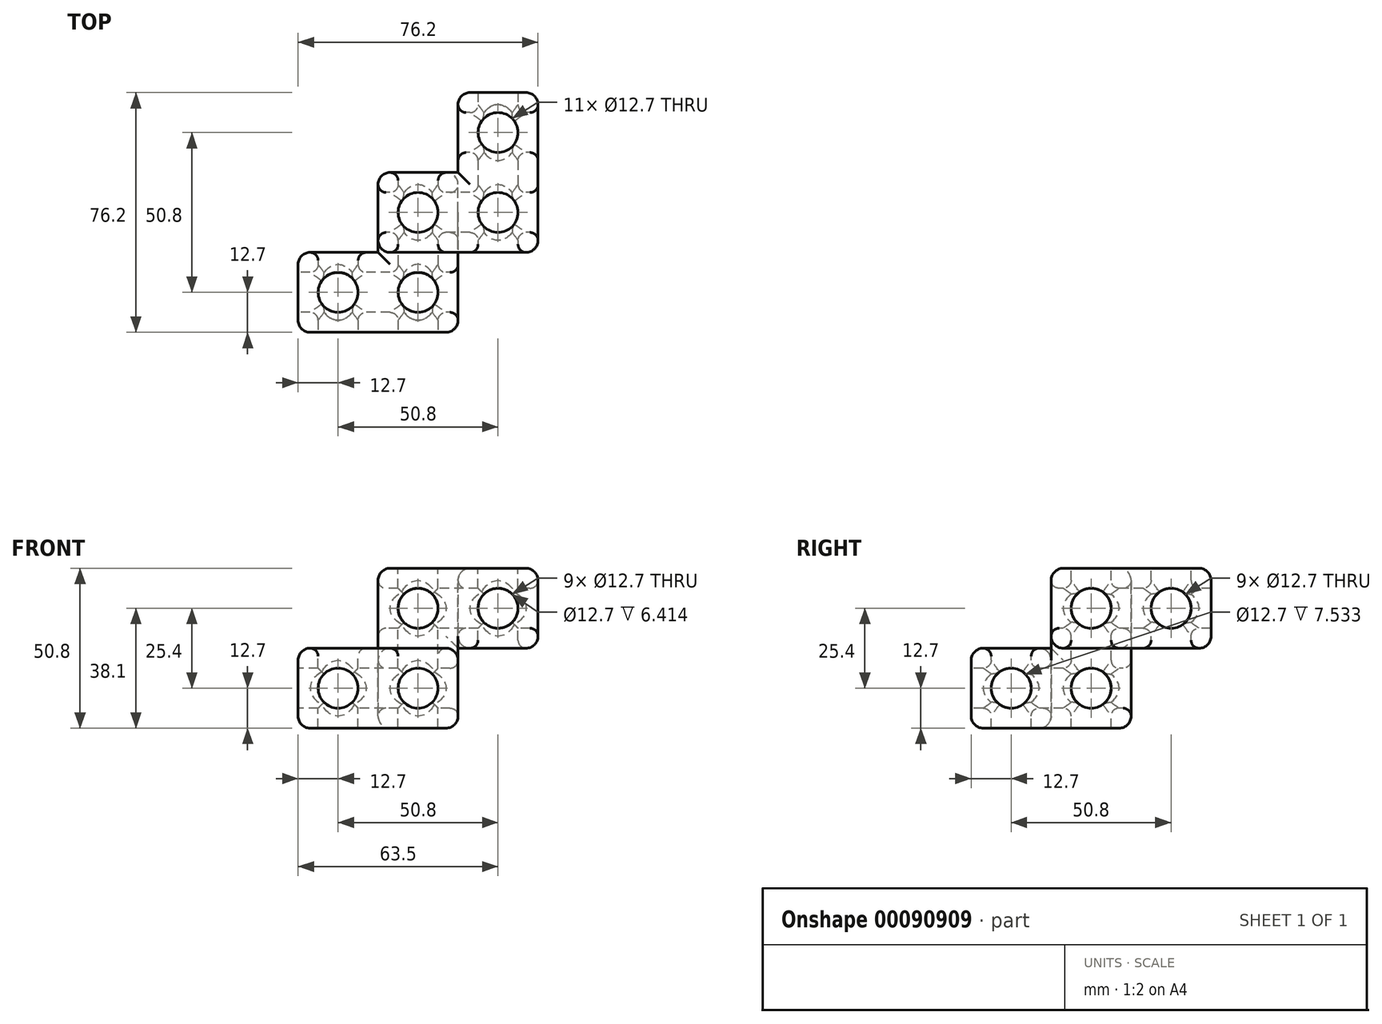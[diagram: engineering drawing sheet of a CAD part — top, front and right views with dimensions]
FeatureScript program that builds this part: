
annotation { "Feature Type Name" : "Feature", "Feature Type Description" : "" }
export const myFeature = defineFeature(function(context is Context, id is Id, definition is map)
    precondition{}
    {
        {
            var Q0;
            Q0=qCreatedBy(makeId("Top.planeOp"),FACE);
            var sketch = newSketch(context, id + "F0", { "sketchPlane" : qUnion([Q0])});
            skLineSegment(sketch, "E0.bottom", {"start": v(0, 0) * mm, "end": v(50.8, 0) * mm});
            skLineSegment(sketch, "E0.right", {"start": v(50.8, 0) * mm, "end": v(50.8, 50.8) * mm});
            skLineSegment(sketch, "E1", {"start": v(0, 25.4) * mm, "end": v(25.4, 25.4) * mm});
            skPoint(sketch, "E1.endSnap0", {"position": v(25.4, 0) * mm});
            skLineSegment(sketch, "E2", {"start": v(25.4, 25.4) * mm, "end": v(25.4, 50.8) * mm});
            skLineSegment(sketch, "E3", {"start": v(0, 0) * mm, "end": v(0, 25.4) * mm});
            skLineSegment(sketch, "E4", {"start": v(25.4, 50.8) * mm, "end": v(50.8, 50.8) * mm});
            skSolve(sketch);
        }
        {
            var Q0;
            Q0 = qSketchRegion(id + "F0", true);
            extrude(context, id + "F1", {"entities" : qUnion([Q0]), "depth" : 25.4 * mm});
        }
        {
            var Q0;
            Q0=makeQuery(id+"F1.opExtrude","CAP_FACE",FACE,{"disambiguationData":[OSD([sQuery(id+"F0.wireOp",EDGE,"E0.bottom"),sQuery(id+"F0.wireOp",EDGE,"E0.right"),sQuery(id+"F0.wireOp",EDGE,"E1"),sQuery(id+"F0.wireOp",EDGE,"E2"),sQuery(id+"F0.wireOp",EDGE,"E3"),sQuery(id+"F0.wireOp",EDGE,"E4")])],"isStart":false});
            var sketch = newSketch(context, id + "F2", { "sketchPlane" : qUnion([Q0])});
            skLineSegment(sketch, "E5.bottom", {"start": v(25.4, 25.4) * mm, "end": v(76.2, 25.4) * mm});
            skLineSegment(sketch, "E5.right", {"start": v(76.2, 25.4) * mm, "end": v(76.2, 76.2) * mm});
            skLineSegment(sketch, "E6.bottom", {"start": v(50.8, 50.8) * mm, "end": v(25.4, 50.8) * mm});
            skLineSegment(sketch, "E6.left", {"start": v(50.8, 50.8) * mm, "end": v(50.8, 76.2) * mm});
            skLineSegment(sketch, "E7", {"start": v(50.8, 76.2) * mm, "end": v(76.2, 76.2) * mm});
            skLineSegment(sketch, "E8", {"start": v(25.4, 25.4) * mm, "end": v(25.4, 50.8) * mm});
            skSolve(sketch);
        }
        {
            var Q0;
            Q0 = qSketchRegion(id + "F2", true);
            extrude(context, id + "F3", {"entities" : qUnion([Q0]), "operationType" : NewBodyOperationType.ADD, "depth" : 25.4 * mm});
        }
        {
            var Q0;
            Q0=makeQuery(id+"F1.opExtrude","SWEPT_FACE",FACE,{"disambiguationData":[OSD([sQuery(id+"F0.wireOp",EDGE,"E0.bottom")])]});
            var sketch = newSketch(context, id + "F4", { "sketchPlane" : qUnion([Q0])});
            skCircle(sketch, "E9", {"center": v(12.7, 12.7) * mm, "radius": 6.35 * mm});
            skCircle(sketch, "E10.0.1.0", {"center": v(12.7, 38.1) * mm, "radius": 6.35 * mm});
            skCircle(sketch, "E10.1.0.0", {"center": v(38.1, 12.7) * mm, "radius": 6.35 * mm});
            skCircle(sketch, "E10.1.1.0", {"center": v(38.1, 38.1) * mm, "radius": 6.35 * mm});
            skCircle(sketch, "E10.2.0.0", {"center": v(63.5, 12.7) * mm, "radius": 6.35 * mm});
            skCircle(sketch, "E10.2.1.0", {"center": v(63.5, 38.1) * mm, "radius": 6.35 * mm});
            skLineSegment(sketch, "E10.direction1", {"start": v(12.7, 12.7) * mm, "end": v(38.1, 12.7) * mm, "construction": true});
            skLineSegment(sketch, "E10.direction2", {"start": v(12.7, 12.7) * mm, "end": v(12.7, 38.1) * mm, "construction": true});
            skSolve(sketch);
        }
        {
            var Q0;
            Q0 = qSketchRegion(id + "F4", true);
            extrude(context, id + "F5", {"entities" : qUnion([Q0]), "operationType" : NewBodyOperationType.REMOVE, "oppositeDirection" : true, "depth" : 76.2 * mm});
        }
        {
            var Q0;
            Q0=makeQuery(id+"F1.opExtrude","SWEPT_FACE",FACE,{"disambiguationData":[OSD([sQuery(id+"F0.wireOp",EDGE,"E0.right")])]});
            var sketch = newSketch(context, id + "F6", { "sketchPlane" : qUnion([Q0])});
            skCircle(sketch, "E11", {"center": v(12.7, 12.7) * mm, "radius": 6.35 * mm});
            skCircle(sketch, "E12.0.1.0", {"center": v(12.7, 38.1) * mm, "radius": 6.35 * mm});
            skCircle(sketch, "E12.1.0.0", {"center": v(38.1, 12.7) * mm, "radius": 6.35 * mm});
            skCircle(sketch, "E12.1.1.0", {"center": v(38.1, 38.1) * mm, "radius": 6.35 * mm});
            skCircle(sketch, "E12.2.0.0", {"center": v(63.5, 12.7) * mm, "radius": 6.35 * mm});
            skCircle(sketch, "E12.2.1.0", {"center": v(63.5, 38.1) * mm, "radius": 6.35 * mm});
            skLineSegment(sketch, "E12.direction1", {"start": v(12.7, 12.7) * mm, "end": v(38.1, 12.7) * mm, "construction": true});
            skLineSegment(sketch, "E12.direction2", {"start": v(12.7, 12.7) * mm, "end": v(12.7, 38.1) * mm, "construction": true});
            skSolve(sketch);
        }
        {
            var Q0;
            Q0 = qSketchRegion(id + "F6", true);
            extrude(context, id + "F7", {"entities" : qUnion([Q0]), "operationType" : NewBodyOperationType.REMOVE, "endBound" : BoundingType.SYMMETRIC, "depth" : 101.6 * mm});
        }
        {
            var Q0;
            Q0=makeQuery(id+"F3.opExtrude","CAP_FACE",FACE,{"disambiguationData":[OSD([sQuery(id+"F2.wireOp",EDGE,"E5.bottom"),sQuery(id+"F2.wireOp",EDGE,"E5.right"),sQuery(id+"F2.wireOp",EDGE,"E6.bottom"),sQuery(id+"F2.wireOp",EDGE,"E6.left"),sQuery(id+"F2.wireOp",EDGE,"E7"),sQuery(id+"F2.wireOp",EDGE,"E8")])],"isStart":false});
            var sketch = newSketch(context, id + "F8", { "sketchPlane" : qUnion([Q0])});
            skCircle(sketch, "E13", {"center": v(63.5, 63.5) * mm, "radius": 6.35 * mm});
            skCircle(sketch, "E14.0.1.0", {"center": v(63.5, 38.1) * mm, "radius": 6.35 * mm});
            skCircle(sketch, "E14.0.2.0", {"center": v(63.5, 12.7) * mm, "radius": 6.35 * mm});
            skCircle(sketch, "E14.1.0.0", {"center": v(38.1, 63.5) * mm, "radius": 6.35 * mm});
            skCircle(sketch, "E14.1.1.0", {"center": v(38.1, 38.1) * mm, "radius": 6.35 * mm});
            skCircle(sketch, "E14.1.2.0", {"center": v(38.1, 12.7) * mm, "radius": 6.35 * mm});
            skCircle(sketch, "E14.2.0.0", {"center": v(12.7, 63.5) * mm, "radius": 6.35 * mm});
            skCircle(sketch, "E14.2.1.0", {"center": v(12.7, 38.1) * mm, "radius": 6.35 * mm});
            skCircle(sketch, "E14.2.2.0", {"center": v(12.7, 12.7) * mm, "radius": 6.35 * mm});
            skLineSegment(sketch, "E14.direction1", {"start": v(63.5, 63.5) * mm, "end": v(38.1, 63.5) * mm, "construction": true});
            skLineSegment(sketch, "E14.direction2", {"start": v(63.5, 63.5) * mm, "end": v(63.5, 38.1) * mm, "construction": true});
            skSolve(sketch);
        }
        {
            var Q0;
            Q0 = qSketchRegion(id + "F8", true);
            extrude(context, id + "F9", {"entities" : qUnion([Q0]), "operationType" : NewBodyOperationType.REMOVE, "oppositeDirection" : true, "depth" : 50.8 * mm});
        }
        {
            var Q0;
            Q0=makeQuery(id+"F9.boolean.opBoolean","COPY",EDGE,{"derivedFrom":makeQuery(id+"F9.opExtrude","CAP_EDGE",EDGE,{"disambiguationData":[OSD([sQuery(id+"F8.wireOp",EDGE,"E14.1.1.0")])],"isStart":true})});
            var Q1;
            Q1=makeQuery(id+"F9.boolean.opBoolean","COPY",EDGE,{"derivedFrom":makeQuery(id+"F9.opExtrude","CAP_EDGE",EDGE,{"disambiguationData":[OSD([sQuery(id+"F8.wireOp",EDGE,"E14.0.1.0")])],"isStart":true})});
            var Q2;
            Q2=makeQuery(id+"F9.boolean.opBoolean","COPY",EDGE,{"derivedFrom":makeQuery(id+"F9.opExtrude","CAP_EDGE",EDGE,{"disambiguationData":[OSD([sQuery(id+"F8.wireOp",EDGE,"E13")])],"isStart":true})});
            var Q3;
            Q3=makeQuery(id+"F5.boolean.opBoolean","INTERSECT",EDGE,{"derivedFrom":[makeQuery(id+"F3.opExtrude","SWEPT_FACE",FACE,{"disambiguationData":[OSD([sQuery(id+"F2.wireOp",EDGE,"E5.bottom")])]}),makeQuery(id+"F5.opExtrude","SWEPT_FACE",FACE,{"disambiguationData":[OSD([sQuery(id+"F4.wireOp",EDGE,"E10.2.1.0")])]})]});
            var Q4;
            Q4=makeQuery(id+"F5.boolean.opBoolean","INTERSECT",EDGE,{"derivedFrom":[makeQuery(id+"F3.opExtrude","SWEPT_FACE",FACE,{"disambiguationData":[OSD([sQuery(id+"F2.wireOp",EDGE,"E5.bottom")])]}),makeQuery(id+"F5.opExtrude","SWEPT_FACE",FACE,{"disambiguationData":[OSD([sQuery(id+"F4.wireOp",EDGE,"E10.1.1.0")])]})]});
            var Q5;
            Q5=makeQuery(id+"F9.boolean.opBoolean","INTERSECT",EDGE,{"derivedFrom":[makeQuery(id+"F1.opExtrude","CAP_FACE",FACE,{"disambiguationData":[OSD([sQuery(id+"F0.wireOp",EDGE,"E0.bottom"),sQuery(id+"F0.wireOp",EDGE,"E0.right"),sQuery(id+"F0.wireOp",EDGE,"E1"),sQuery(id+"F0.wireOp",EDGE,"E2"),sQuery(id+"F0.wireOp",EDGE,"E3"),sQuery(id+"F0.wireOp",EDGE,"E4")])],"isStart":false}),makeQuery(id+"F9.opExtrude","SWEPT_FACE",FACE,{"disambiguationData":[OSD([sQuery(id+"F8.wireOp",EDGE,"E14.1.2.0")])]})]});
            var Q6;
            Q6=makeQuery(id+"F9.boolean.opBoolean","INTERSECT",EDGE,{"derivedFrom":[makeQuery(id+"F1.opExtrude","CAP_FACE",FACE,{"disambiguationData":[OSD([sQuery(id+"F0.wireOp",EDGE,"E0.bottom"),sQuery(id+"F0.wireOp",EDGE,"E0.right"),sQuery(id+"F0.wireOp",EDGE,"E1"),sQuery(id+"F0.wireOp",EDGE,"E2"),sQuery(id+"F0.wireOp",EDGE,"E3"),sQuery(id+"F0.wireOp",EDGE,"E4")])],"isStart":false}),makeQuery(id+"F9.opExtrude","SWEPT_FACE",FACE,{"disambiguationData":[OSD([sQuery(id+"F8.wireOp",EDGE,"E14.2.2.0")])]})]});
            var Q7;
            Q7=makeQuery(id+"F5.boolean.opBoolean","COPY",EDGE,{"derivedFrom":makeQuery(id+"F5.opExtrude","CAP_EDGE",EDGE,{"disambiguationData":[OSD([sQuery(id+"F4.wireOp",EDGE,"E9")])],"isStart":true})});
            var Q8;
            Q8=makeQuery(id+"F5.boolean.opBoolean","COPY",EDGE,{"derivedFrom":makeQuery(id+"F5.opExtrude","CAP_EDGE",EDGE,{"disambiguationData":[OSD([sQuery(id+"F4.wireOp",EDGE,"E10.1.0.0")])],"isStart":true})});
            var Q9;
            Q9=makeQuery(id+"F7.boolean.opBoolean","INTERSECT",EDGE,{"derivedFrom":[makeQuery(id+"F1.opExtrude","SWEPT_FACE",FACE,{"disambiguationData":[OSD([sQuery(id+"F0.wireOp",EDGE,"E0.right")])]}),makeQuery(id+"F7.opExtrude","SWEPT_FACE",FACE,{"disambiguationData":[OSD([sQuery(id+"F6.wireOp",EDGE,"E11")])]})]});
            var Q10;
            Q10=makeQuery(id+"F7.boolean.opBoolean","INTERSECT",EDGE,{"derivedFrom":[makeQuery(id+"F1.opExtrude","SWEPT_FACE",FACE,{"disambiguationData":[OSD([sQuery(id+"F0.wireOp",EDGE,"E0.right")])]}),makeQuery(id+"F7.opExtrude","SWEPT_FACE",FACE,{"disambiguationData":[OSD([sQuery(id+"F6.wireOp",EDGE,"E12.1.0.0")])]})]});
            var Q11;
            Q11=makeQuery(id+"F7.boolean.opBoolean","INTERSECT",EDGE,{"derivedFrom":[makeQuery(id+"F3.opExtrude","SWEPT_FACE",FACE,{"disambiguationData":[OSD([sQuery(id+"F2.wireOp",EDGE,"E5.right")])]}),makeQuery(id+"F7.opExtrude","SWEPT_FACE",FACE,{"disambiguationData":[OSD([sQuery(id+"F6.wireOp",EDGE,"E12.1.1.0")])]})]});
            var Q12;
            Q12=makeQuery(id+"F9.boolean.opBoolean","INTERSECT",EDGE,{"derivedFrom":[makeQuery(id+"F3.opExtrude","CAP_FACE",FACE,{"disambiguationData":[OSD([sQuery(id+"F2.wireOp",EDGE,"E5.bottom"),sQuery(id+"F2.wireOp",EDGE,"E5.right"),sQuery(id+"F2.wireOp",EDGE,"E6.bottom"),sQuery(id+"F2.wireOp",EDGE,"E6.left"),sQuery(id+"F2.wireOp",EDGE,"E7"),sQuery(id+"F2.wireOp",EDGE,"E8")])],"isStart":true}),makeQuery(id+"F9.opExtrude","SWEPT_FACE",FACE,{"disambiguationData":[OSD([sQuery(id+"F8.wireOp",EDGE,"E14.0.1.0")])]})]});
            var Q13;
            Q13=makeQuery(id+"F9.boolean.opBoolean","INTERSECT",EDGE,{"derivedFrom":[makeQuery(id+"F3.opExtrude","CAP_FACE",FACE,{"disambiguationData":[OSD([sQuery(id+"F2.wireOp",EDGE,"E5.bottom"),sQuery(id+"F2.wireOp",EDGE,"E5.right"),sQuery(id+"F2.wireOp",EDGE,"E6.bottom"),sQuery(id+"F2.wireOp",EDGE,"E6.left"),sQuery(id+"F2.wireOp",EDGE,"E7"),sQuery(id+"F2.wireOp",EDGE,"E8")])],"isStart":true}),makeQuery(id+"F9.opExtrude","SWEPT_FACE",FACE,{"disambiguationData":[OSD([sQuery(id+"F8.wireOp",EDGE,"E13")])]})]});
            var Q14;
            Q14=makeQuery(id+"F9.boolean.opBoolean","COPY",EDGE,{"derivedFrom":makeQuery(id+"F9.opExtrude","CAP_EDGE",EDGE,{"disambiguationData":[OSD([sQuery(id+"F8.wireOp",EDGE,"E14.1.1.0")])],"isStart":false})});
            var Q15;
            Q15=makeQuery(id+"F9.boolean.opBoolean","COPY",EDGE,{"derivedFrom":makeQuery(id+"F9.opExtrude","CAP_EDGE",EDGE,{"disambiguationData":[OSD([sQuery(id+"F8.wireOp",EDGE,"E14.1.2.0")])],"isStart":false})});
            var Q16;
            Q16=makeQuery(id+"F9.boolean.opBoolean","COPY",EDGE,{"derivedFrom":makeQuery(id+"F9.opExtrude","CAP_EDGE",EDGE,{"disambiguationData":[OSD([sQuery(id+"F8.wireOp",EDGE,"E14.2.2.0")])],"isStart":false})});
            var Q17;
            Q17=makeQuery(id+"F7.boolean.opBoolean","COPY",EDGE,{"derivedFrom":makeQuery(id+"F7.opExtrude","CAP_EDGE",EDGE,{"disambiguationData":[OSD([sQuery(id+"F6.wireOp",EDGE,"E11")])],"isStart":true})});
            var Q18;
            Q18=makeQuery(id+"F5.boolean.opBoolean","INTERSECT",EDGE,{"derivedFrom":[makeQuery(id+"F1.opExtrude","SWEPT_FACE",FACE,{"disambiguationData":[OSD([sQuery(id+"F0.wireOp",EDGE,"E1")])]}),makeQuery(id+"F5.opExtrude","SWEPT_FACE",FACE,{"disambiguationData":[OSD([sQuery(id+"F4.wireOp",EDGE,"E9")])]})]});
            var Q19;
            Q19=makeQuery(id+"F7.boolean.opBoolean","INTERSECT",EDGE,{"derivedFrom":[makeQuery(id+"F3.boolean.opBoolean","MERGE",FACE,{"derivedFrom":[makeQuery(id+"F1.opExtrude","SWEPT_FACE",FACE,{"disambiguationData":[OSD([sQuery(id+"F0.wireOp",EDGE,"E2")])]}),makeQuery(id+"F3.opExtrude","SWEPT_FACE",FACE,{"disambiguationData":[OSD([sQuery(id+"F2.wireOp",EDGE,"E8")])]})]}),makeQuery(id+"F7.opExtrude","SWEPT_FACE",FACE,{"disambiguationData":[OSD([sQuery(id+"F6.wireOp",EDGE,"E12.1.0.0")])]})]});
            var Q20;
            Q20=makeQuery(id+"F7.boolean.opBoolean","INTERSECT",EDGE,{"derivedFrom":[makeQuery(id+"F3.boolean.opBoolean","MERGE",FACE,{"derivedFrom":[makeQuery(id+"F1.opExtrude","SWEPT_FACE",FACE,{"disambiguationData":[OSD([sQuery(id+"F0.wireOp",EDGE,"E2")])]}),makeQuery(id+"F3.opExtrude","SWEPT_FACE",FACE,{"disambiguationData":[OSD([sQuery(id+"F2.wireOp",EDGE,"E8")])]})]}),makeQuery(id+"F7.opExtrude","SWEPT_FACE",FACE,{"disambiguationData":[OSD([sQuery(id+"F6.wireOp",EDGE,"E12.1.1.0")])]})]});
            var Q21;
            Q21=makeQuery(id+"F5.boolean.opBoolean","INTERSECT",EDGE,{"derivedFrom":[makeQuery(id+"F3.boolean.opBoolean","MERGE",FACE,{"derivedFrom":[makeQuery(id+"F1.opExtrude","SWEPT_FACE",FACE,{"disambiguationData":[OSD([sQuery(id+"F0.wireOp",EDGE,"E4")])]}),makeQuery(id+"F3.opExtrude","SWEPT_FACE",FACE,{"disambiguationData":[OSD([sQuery(id+"F2.wireOp",EDGE,"E6.bottom")])]})]}),makeQuery(id+"F5.opExtrude","SWEPT_FACE",FACE,{"disambiguationData":[OSD([sQuery(id+"F4.wireOp",EDGE,"E10.1.1.0")])]})]});
            var Q22;
            Q22=makeQuery(id+"F5.boolean.opBoolean","INTERSECT",EDGE,{"derivedFrom":[makeQuery(id+"F3.boolean.opBoolean","MERGE",FACE,{"derivedFrom":[makeQuery(id+"F1.opExtrude","SWEPT_FACE",FACE,{"disambiguationData":[OSD([sQuery(id+"F0.wireOp",EDGE,"E4")])]}),makeQuery(id+"F3.opExtrude","SWEPT_FACE",FACE,{"disambiguationData":[OSD([sQuery(id+"F2.wireOp",EDGE,"E6.bottom")])]})]}),makeQuery(id+"F5.opExtrude","SWEPT_FACE",FACE,{"disambiguationData":[OSD([sQuery(id+"F4.wireOp",EDGE,"E10.1.0.0")])]})]});
            var Q23;
            Q23=makeQuery(id+"F7.boolean.opBoolean","INTERSECT",EDGE,{"derivedFrom":[makeQuery(id+"F3.opExtrude","SWEPT_FACE",FACE,{"disambiguationData":[OSD([sQuery(id+"F2.wireOp",EDGE,"E6.left")])]}),makeQuery(id+"F7.opExtrude","SWEPT_FACE",FACE,{"disambiguationData":[OSD([sQuery(id+"F6.wireOp",EDGE,"E12.2.1.0")])]})]});
            var Q24;
            Q24=makeQuery(id+"F5.boolean.opBoolean","COPY",EDGE,{"derivedFrom":makeQuery(id+"F5.opExtrude","CAP_EDGE",EDGE,{"disambiguationData":[OSD([sQuery(id+"F4.wireOp",EDGE,"E10.2.1.0")])],"isStart":false})});
            var Q25;
            Q25=makeQuery(id+"F7.boolean.opBoolean","INTERSECT",EDGE,{"derivedFrom":[makeQuery(id+"F3.opExtrude","SWEPT_FACE",FACE,{"disambiguationData":[OSD([sQuery(id+"F2.wireOp",EDGE,"E5.right")])]}),makeQuery(id+"F7.opExtrude","SWEPT_FACE",FACE,{"disambiguationData":[OSD([sQuery(id+"F6.wireOp",EDGE,"E12.2.1.0")])]})]});
            fillet(context, id + "F10", {"entities" : qUnion([Q0, Q1, Q2, Q3, Q4, Q5, Q6, Q7, Q8, Q9, Q10, Q11, Q12, Q13, Q14, Q15, Q16, Q17, Q18, Q19, Q20, Q21, Q22, Q23, Q24, Q25]), "radius" : 2.54 * mm, "tangentPropagation" : true, "allowEdgeOverflow" : false});
        }
        {
            var Q0;
            Q0=makeQuery(id+"F1.opExtrude","CAP_EDGE",EDGE,{"disambiguationData":[OSD([sQuery(id+"F0.wireOp",EDGE,"E1")])],"isStart":true});
            var Q1;
            Q1=makeQuery(id+"F1.opExtrude","SWEPT_EDGE",EDGE,{"disambiguationData":[OSD([sQuery(id+"F0.wireOp",EDGE,"E1"),sQuery(id+"F0.wireOp",EDGE,"E3")])]});
            var Q2;
            Q2=makeQuery(id+"F1.opExtrude","CAP_EDGE",EDGE,{"disambiguationData":[OSD([sQuery(id+"F0.wireOp",EDGE,"E3")])],"isStart":true});
            var Q3;
            Q3=makeQuery(id+"F1.opExtrude","SWEPT_EDGE",EDGE,{"disambiguationData":[OSD([sQuery(id+"F0.wireOp",EDGE,"E0.bottom"),sQuery(id+"F0.wireOp",EDGE,"E3")])]});
            var Q4;
            Q4=makeQuery(id+"F1.opExtrude","CAP_EDGE",EDGE,{"disambiguationData":[OSD([sQuery(id+"F0.wireOp",EDGE,"E3")])],"isStart":false});
            var Q5;
            Q5=makeQuery(id+"F1.opExtrude","CAP_EDGE",EDGE,{"disambiguationData":[OSD([sQuery(id+"F0.wireOp",EDGE,"E0.bottom")])],"isStart":true});
            var Q6;
            Q6=makeQuery(id+"F1.opExtrude","CAP_EDGE",EDGE,{"disambiguationData":[OSD([sQuery(id+"F0.wireOp",EDGE,"E0.right")])],"isStart":true});
            var Q7;
            Q7=makeQuery(id+"F1.opExtrude","CAP_EDGE",EDGE,{"disambiguationData":[OSD([sQuery(id+"F0.wireOp",EDGE,"E2")])],"isStart":true});
            var Q8;
            Q8=makeQuery(id+"F3.boolean.opBoolean","MERGE",EDGE,{"derivedFrom":[makeQuery(id+"F1.opExtrude","SWEPT_EDGE",EDGE,{"disambiguationData":[OSD([sQuery(id+"F0.wireOp",EDGE,"E2"),sQuery(id+"F0.wireOp",EDGE,"E4")])]}),makeQuery(id+"F3.opExtrude","SWEPT_EDGE",EDGE,{"disambiguationData":[OSD([sQuery(id+"F2.wireOp",EDGE,"E6.bottom"),sQuery(id+"F2.wireOp",EDGE,"E8")])]})]});
            var Q9;
            Q9=makeQuery(id+"F1.opExtrude","CAP_EDGE",EDGE,{"disambiguationData":[OSD([sQuery(id+"F0.wireOp",EDGE,"E0.bottom")])],"isStart":false});
            var Q10;
            Q10=makeQuery(id+"F3.opExtrude","SWEPT_EDGE",EDGE,{"disambiguationData":[OSD([sQuery(id+"F2.wireOp",EDGE,"E5.bottom"),sQuery(id+"F2.wireOp",EDGE,"E5.right")])]});
            var Q11;
            Q11=makeQuery(id+"F3.opExtrude","CAP_EDGE",EDGE,{"disambiguationData":[OSD([sQuery(id+"F2.wireOp",EDGE,"E5.right")])],"isStart":false});
            var Q12;
            Q12=makeQuery(id+"F3.opExtrude","CAP_EDGE",EDGE,{"disambiguationData":[OSD([sQuery(id+"F2.wireOp",EDGE,"E5.right")])],"isStart":true});
            var Q13;
            Q13=makeQuery(id+"F3.opExtrude","SWEPT_EDGE",EDGE,{"disambiguationData":[OSD([sQuery(id+"F2.wireOp",EDGE,"E5.right"),sQuery(id+"F2.wireOp",EDGE,"E7")])]});
            var Q14;
            Q14=makeQuery(id+"F3.opExtrude","CAP_EDGE",EDGE,{"disambiguationData":[OSD([sQuery(id+"F2.wireOp",EDGE,"E7")])],"isStart":true});
            var Q15;
            Q15=makeQuery(id+"F3.opExtrude","CAP_EDGE",EDGE,{"disambiguationData":[OSD([sQuery(id+"F2.wireOp",EDGE,"E7")])],"isStart":false});
            var Q16;
            Q16=makeQuery(id+"F3.opExtrude","SWEPT_EDGE",EDGE,{"disambiguationData":[OSD([sQuery(id+"F2.wireOp",EDGE,"E6.left"),sQuery(id+"F2.wireOp",EDGE,"E7")])]});
            var Q17;
            Q17=makeQuery(id+"F3.opExtrude","CAP_EDGE",EDGE,{"disambiguationData":[OSD([sQuery(id+"F2.wireOp",EDGE,"E6.left")])],"isStart":false});
            var Q18;
            Q18=makeQuery(id+"F3.opExtrude","CAP_EDGE",EDGE,{"disambiguationData":[OSD([sQuery(id+"F2.wireOp",EDGE,"E5.bottom")])],"isStart":false});
            var Q19;
            Q19=makeQuery(id+"F3.opExtrude","CAP_EDGE",EDGE,{"disambiguationData":[OSD([sQuery(id+"F2.wireOp",EDGE,"E8")])],"isStart":false});
            var Q20;
            Q20=makeQuery(id+"F1.opExtrude","SWEPT_EDGE",EDGE,{"disambiguationData":[OSD([sQuery(id+"F0.wireOp",EDGE,"E0.bottom"),sQuery(id+"F0.wireOp",EDGE,"E0.right")])]});
            var Q21;
            {var subQ0=sQuery(id+"F0.wireOp",EDGE,"E0.right");var subQ1=sQuery(id+"F0.wireOp",EDGE,"E0.bottom");Q21=makeQuery(id+"F3.boolean.opBoolean","SPLIT",EDGE,{"disambiguationData":[TD([makeQuery(id+"F1.opExtrude","SWEPT_FACE",FACE,{"disambiguationData":[OSD([subQ1])]})])],"derivedFrom":makeQuery(id+"F1.opExtrude","CAP_EDGE",EDGE,{"disambiguationData":[OSD([subQ0])],"isStart":false})});}
            var Q22;
            Q22=makeQuery(id+"F1.opExtrude","SWEPT_EDGE",EDGE,{"disambiguationData":[OSD([sQuery(id+"F0.wireOp",EDGE,"E0.right"),sQuery(id+"F0.wireOp",EDGE,"E4")])]});
            var Q23;
            Q23=makeQuery(id+"F3.opExtrude","CAP_EDGE",EDGE,{"disambiguationData":[OSD([sQuery(id+"F2.wireOp",EDGE,"E6.bottom")])],"isStart":false});
            var Q24;
            Q24=makeQuery(id+"F1.opExtrude","CAP_EDGE",EDGE,{"disambiguationData":[OSD([sQuery(id+"F0.wireOp",EDGE,"E4")])],"isStart":true});
            fillet(context, id + "F11", {"entities" : qUnion([Q0, Q1, Q2, Q3, Q4, Q5, Q6, Q7, Q8, Q9, Q10, Q11, Q12, Q13, Q14, Q15, Q16, Q17, Q18, Q19, Q20, Q21, Q22, Q23, Q24]), "radius" : 3.8 * mm, "tangentPropagation" : true, "allowEdgeOverflow" : false});
        }
        {
            var Q0;
            Q0=makeQuery(id+"F3.opExtrude","CAP_EDGE",EDGE,{"disambiguationData":[OSD([sQuery(id+"F2.wireOp",EDGE,"E6.left")])],"isStart":true});
            var Q1;
            {var subQ0=sQuery(id+"F0.wireOp",EDGE,"E0.right");Q1=makeQuery(id+"F11.opFillet","TWEAK_EDGE",EDGE,{"derivedFrom":[makeQuery(id+"F3.boolean.opBoolean","MERGE",VERTEX,{"derivedFrom":[makeQuery(id+"F1.opExtrude","CAP_VERTEX",VERTEX,{"disambiguationData":[OSD([subQ0,sQuery(id+"F0.wireOp",EDGE,"E4")])],"isStart":false}),makeQuery(id+"F3.opExtrude","CAP_VERTEX",VERTEX,{"disambiguationData":[OSD([subQ0,sQuery(id+"F2.wireOp",EDGE,"E6.bottom"),sQuery(id+"F2.wireOp",EDGE,"E6.left")])],"isStart":true})]})]});}
            var Q2;
            Q2=makeQuery(id+"F1.opExtrude","CAP_EDGE",EDGE,{"disambiguationData":[OSD([sQuery(id+"F0.wireOp",EDGE,"E1")])],"isStart":false});
            var Q3;
            {var subQ0=sQuery(id+"F2.wireOp",EDGE,"E5.bottom");var subQ1=sQuery(id+"F0.wireOp",EDGE,"E0.right");Q3=makeQuery(id+"F11.opFillet","TWEAK_EDGE",EDGE,{"derivedFrom":[makeQuery(id+"F3.boolean.opBoolean","TWEAK_VERTEX",VERTEX,{"derivedFrom":[makeQuery(id+"F1.opExtrude","CAP_FACE",FACE,{"disambiguationData":[OSD([sQuery(id+"F0.wireOp",EDGE,"E0.bottom"),subQ1,sQuery(id+"F0.wireOp",EDGE,"E1"),sQuery(id+"F0.wireOp",EDGE,"E2"),sQuery(id+"F0.wireOp",EDGE,"E3"),sQuery(id+"F0.wireOp",EDGE,"E4")])],"isStart":false}),makeQuery(id+"F1.opExtrude","SWEPT_FACE",FACE,{"disambiguationData":[OSD([subQ1])]}),makeQuery(id+"F3.opExtrude","SWEPT_FACE",FACE,{"disambiguationData":[OSD([subQ0])]}),makeQuery(id+"F3.opExtrude","CAP_FACE",FACE,{"disambiguationData":[OSD([subQ0,sQuery(id+"F2.wireOp",EDGE,"E5.right"),sQuery(id+"F2.wireOp",EDGE,"E6.bottom"),sQuery(id+"F2.wireOp",EDGE,"E6.left"),sQuery(id+"F2.wireOp",EDGE,"E7"),sQuery(id+"F2.wireOp",EDGE,"E8")])],"isStart":true})]})]});}
            var Q4;
            {var subQ0=sQuery(id+"F2.wireOp",EDGE,"E5.right");var subQ1=sQuery(id+"F2.wireOp",EDGE,"E5.bottom");Q4=makeQuery(id+"F3.boolean.opBoolean","SPLIT",EDGE,{"disambiguationData":[TD([makeQuery(id+"F3.opExtrude","SWEPT_FACE",FACE,{"disambiguationData":[OSD([subQ0])]})])],"derivedFrom":makeQuery(id+"F3.opExtrude","CAP_EDGE",EDGE,{"disambiguationData":[OSD([subQ1])],"isStart":true})});}
            fillet(context, id + "F12", {"entities" : qUnion([Q0, Q1, Q2, Q3, Q4]), "radius" : 3.8 * mm, "tangentPropagation" : true, "allowEdgeOverflow" : false});
        }
        {
            var Q0;
            Q0=makeQuery(id+"F3.opExtrude","SWEPT_EDGE",EDGE,{"disambiguationData":[OSD([sQuery(id+"F0.wireOp",EDGE,"E1"),sQuery(id+"F2.wireOp",EDGE,"E5.bottom"),sQuery(id+"F2.wireOp",EDGE,"E8")])]});
            var Q1;
            {var subQ0=sQuery(id+"F0.wireOp",EDGE,"E1");Q1=makeQuery(id+"F12.opFillet","TWEAK_EDGE",EDGE,{"derivedFrom":[makeQuery(id+"F3.boolean.opBoolean","MERGE",VERTEX,{"derivedFrom":[makeQuery(id+"F1.opExtrude","CAP_VERTEX",VERTEX,{"disambiguationData":[OSD([subQ0,sQuery(id+"F0.wireOp",EDGE,"E2")])],"isStart":false}),makeQuery(id+"F3.opExtrude","CAP_VERTEX",VERTEX,{"disambiguationData":[OSD([subQ0,sQuery(id+"F2.wireOp",EDGE,"E5.bottom"),sQuery(id+"F2.wireOp",EDGE,"E8")])],"isStart":true})]})]});}
            fillet(context, id + "F13", {"entities" : qUnion([Q0, Q1]), "radius" : 3.8 * mm, "tangentPropagation" : true, "allowEdgeOverflow" : false});
        }
        {
            var Q0;
            Q0=makeQuery(id+"F9.boolean.opBoolean","INTERSECT",EDGE,{"disambiguationData":[OD(0.0)],"derivedFrom":[makeQuery(id+"F7.boolean.opBoolean","COPY",FACE,{"disambiguationData":[OD(0.0)],"derivedFrom":makeQuery(id+"F7.opExtrude","SWEPT_FACE",FACE,{"disambiguationData":[OSD([sQuery(id+"F6.wireOp",EDGE,"E11")])]})}),makeQuery(id+"F9.opExtrude","SWEPT_FACE",FACE,{"disambiguationData":[OSD([sQuery(id+"F8.wireOp",EDGE,"E14.2.2.0")])]})]});
            var Q1;
            Q1=makeQuery(id+"F7.boolean.opBoolean","INTERSECT",EDGE,{"disambiguationData":[OD(0.0)],"derivedFrom":[makeQuery(id+"F5.boolean.opBoolean","COPY",FACE,{"derivedFrom":makeQuery(id+"F5.opExtrude","SWEPT_FACE",FACE,{"disambiguationData":[OSD([sQuery(id+"F4.wireOp",EDGE,"E9")])]})}),makeQuery(id+"F7.opExtrude","SWEPT_FACE",FACE,{"disambiguationData":[OSD([sQuery(id+"F6.wireOp",EDGE,"E11")])]})]});
            var Q2;
            {var subQ0=makeQuery(id+"F5.boolean.opBoolean","COPY",FACE,{"derivedFrom":makeQuery(id+"F5.opExtrude","SWEPT_FACE",FACE,{"disambiguationData":[OSD([sQuery(id+"F4.wireOp",EDGE,"E9")])]})});Q2=makeQuery(id+"F9.boolean.opBoolean","INTERSECT",EDGE,{"disambiguationData":[OD(0.0)],"derivedFrom":[makeQuery(id+"F7.boolean.opBoolean","SPLIT",FACE,{"disambiguationData":[TD([makeQuery(id+"F1.opExtrude","SWEPT_FACE",FACE,{"disambiguationData":[OSD([sQuery(id+"F0.wireOp",EDGE,"E0.bottom")])]})])],"derivedFrom":subQ0}),makeQuery(id+"F9.opExtrude","SWEPT_FACE",FACE,{"disambiguationData":[OSD([sQuery(id+"F8.wireOp",EDGE,"E14.2.2.0")])]})]});}
            var Q3;
            Q3=makeQuery(id+"F9.boolean.opBoolean","INTERSECT",EDGE,{"disambiguationData":[OD(0.0)],"derivedFrom":[makeQuery(id+"F7.boolean.opBoolean","COPY",FACE,{"disambiguationData":[OD(2.0)],"derivedFrom":makeQuery(id+"F7.opExtrude","SWEPT_FACE",FACE,{"disambiguationData":[OSD([sQuery(id+"F6.wireOp",EDGE,"E11")])]})}),makeQuery(id+"F9.opExtrude","SWEPT_FACE",FACE,{"disambiguationData":[OSD([sQuery(id+"F8.wireOp",EDGE,"E14.1.2.0")])]})]});
            var Q4;
            Q4=makeQuery(id+"F7.boolean.opBoolean","INTERSECT",EDGE,{"disambiguationData":[OD(1.0)],"derivedFrom":[makeQuery(id+"F5.boolean.opBoolean","COPY",FACE,{"derivedFrom":makeQuery(id+"F5.opExtrude","SWEPT_FACE",FACE,{"disambiguationData":[OSD([sQuery(id+"F4.wireOp",EDGE,"E10.1.0.0")])]})}),makeQuery(id+"F7.opExtrude","SWEPT_FACE",FACE,{"disambiguationData":[OSD([sQuery(id+"F6.wireOp",EDGE,"E11")])]})]});
            var Q5;
            {var subQ0=makeQuery(id+"F5.boolean.opBoolean","COPY",FACE,{"derivedFrom":makeQuery(id+"F5.opExtrude","SWEPT_FACE",FACE,{"disambiguationData":[OSD([sQuery(id+"F4.wireOp",EDGE,"E10.1.0.0")])]})});Q5=makeQuery(id+"F9.boolean.opBoolean","INTERSECT",EDGE,{"disambiguationData":[OD(0.0)],"derivedFrom":[makeQuery(id+"F7.boolean.opBoolean","SPLIT",FACE,{"disambiguationData":[TD([makeQuery(id+"F1.opExtrude","SWEPT_FACE",FACE,{"disambiguationData":[OSD([sQuery(id+"F0.wireOp",EDGE,"E0.bottom")])]}),subQ0,makeQuery(id+"F7.opExtrude","SWEPT_FACE",FACE,{"disambiguationData":[OSD([sQuery(id+"F6.wireOp",EDGE,"E11")])]})])],"derivedFrom":subQ0}),makeQuery(id+"F9.opExtrude","SWEPT_FACE",FACE,{"disambiguationData":[OSD([sQuery(id+"F8.wireOp",EDGE,"E14.1.2.0")])]})]});}
            var Q6;
            Q6=makeQuery(id+"F9.boolean.opBoolean","INTERSECT",EDGE,{"disambiguationData":[OD(1.0)],"derivedFrom":[makeQuery(id+"F7.boolean.opBoolean","COPY",FACE,{"disambiguationData":[OD(2.0)],"derivedFrom":makeQuery(id+"F7.opExtrude","SWEPT_FACE",FACE,{"disambiguationData":[OSD([sQuery(id+"F6.wireOp",EDGE,"E11")])]})}),makeQuery(id+"F9.opExtrude","SWEPT_FACE",FACE,{"disambiguationData":[OSD([sQuery(id+"F8.wireOp",EDGE,"E14.1.2.0")])]})]});
            var Q7;
            Q7=makeQuery(id+"F9.boolean.opBoolean","INTERSECT",EDGE,{"disambiguationData":[OD(0.0)],"derivedFrom":[makeQuery(id+"F7.boolean.opBoolean","COPY",FACE,{"disambiguationData":[OD(1.0)],"derivedFrom":makeQuery(id+"F7.opExtrude","SWEPT_FACE",FACE,{"disambiguationData":[OSD([sQuery(id+"F6.wireOp",EDGE,"E11")])]})}),makeQuery(id+"F9.opExtrude","SWEPT_FACE",FACE,{"disambiguationData":[OSD([sQuery(id+"F8.wireOp",EDGE,"E14.1.2.0")])]})]});
            var Q8;
            Q8=makeQuery(id+"F7.boolean.opBoolean","INTERSECT",EDGE,{"disambiguationData":[OD(2.0)],"derivedFrom":[makeQuery(id+"F5.boolean.opBoolean","COPY",FACE,{"derivedFrom":makeQuery(id+"F5.opExtrude","SWEPT_FACE",FACE,{"disambiguationData":[OSD([sQuery(id+"F4.wireOp",EDGE,"E9")])]})}),makeQuery(id+"F7.opExtrude","SWEPT_FACE",FACE,{"disambiguationData":[OSD([sQuery(id+"F6.wireOp",EDGE,"E11")])]})]});
            var Q9;
            Q9=makeQuery(id+"F9.boolean.opBoolean","INTERSECT",EDGE,{"disambiguationData":[OD(1.0)],"derivedFrom":[makeQuery(id+"F7.boolean.opBoolean","COPY",FACE,{"disambiguationData":[OD(0.0)],"derivedFrom":makeQuery(id+"F7.opExtrude","SWEPT_FACE",FACE,{"disambiguationData":[OSD([sQuery(id+"F6.wireOp",EDGE,"E11")])]})}),makeQuery(id+"F9.opExtrude","SWEPT_FACE",FACE,{"disambiguationData":[OSD([sQuery(id+"F8.wireOp",EDGE,"E14.2.2.0")])]})]});
            var Q10;
            {var subQ0=makeQuery(id+"F5.boolean.opBoolean","COPY",FACE,{"derivedFrom":makeQuery(id+"F5.opExtrude","SWEPT_FACE",FACE,{"disambiguationData":[OSD([sQuery(id+"F4.wireOp",EDGE,"E9")])]})});Q10=makeQuery(id+"F9.boolean.opBoolean","INTERSECT",EDGE,{"disambiguationData":[OD(1.0)],"derivedFrom":[makeQuery(id+"F7.boolean.opBoolean","SPLIT",FACE,{"disambiguationData":[TD([makeQuery(id+"F1.opExtrude","SWEPT_FACE",FACE,{"disambiguationData":[OSD([sQuery(id+"F0.wireOp",EDGE,"E1")])]})])],"derivedFrom":subQ0}),makeQuery(id+"F9.opExtrude","SWEPT_FACE",FACE,{"disambiguationData":[OSD([sQuery(id+"F8.wireOp",EDGE,"E14.2.2.0")])]})]});}
            var Q11;
            {var subQ0=makeQuery(id+"F5.boolean.opBoolean","COPY",FACE,{"derivedFrom":makeQuery(id+"F5.opExtrude","SWEPT_FACE",FACE,{"disambiguationData":[OSD([sQuery(id+"F4.wireOp",EDGE,"E9")])]})});Q11=makeQuery(id+"F9.boolean.opBoolean","INTERSECT",EDGE,{"disambiguationData":[OD(0.0)],"derivedFrom":[makeQuery(id+"F7.boolean.opBoolean","SPLIT",FACE,{"disambiguationData":[TD([makeQuery(id+"F1.opExtrude","SWEPT_FACE",FACE,{"disambiguationData":[OSD([sQuery(id+"F0.wireOp",EDGE,"E1")])]})])],"derivedFrom":subQ0}),makeQuery(id+"F9.opExtrude","SWEPT_FACE",FACE,{"disambiguationData":[OSD([sQuery(id+"F8.wireOp",EDGE,"E14.2.2.0")])]})]});}
            var Q12;
            Q12=makeQuery(id+"F7.boolean.opBoolean","INTERSECT",EDGE,{"disambiguationData":[OD(0.0)],"derivedFrom":[makeQuery(id+"F5.boolean.opBoolean","COPY",FACE,{"derivedFrom":makeQuery(id+"F5.opExtrude","SWEPT_FACE",FACE,{"disambiguationData":[OSD([sQuery(id+"F4.wireOp",EDGE,"E10.1.0.0")])]})}),makeQuery(id+"F7.opExtrude","SWEPT_FACE",FACE,{"disambiguationData":[OSD([sQuery(id+"F6.wireOp",EDGE,"E11")])]})]});
            var Q13;
            Q13=makeQuery(id+"F9.boolean.opBoolean","INTERSECT",EDGE,{"disambiguationData":[OD(1.0)],"derivedFrom":[makeQuery(id+"F7.boolean.opBoolean","COPY",FACE,{"disambiguationData":[OD(1.0)],"derivedFrom":makeQuery(id+"F7.opExtrude","SWEPT_FACE",FACE,{"disambiguationData":[OSD([sQuery(id+"F6.wireOp",EDGE,"E11")])]})}),makeQuery(id+"F9.opExtrude","SWEPT_FACE",FACE,{"disambiguationData":[OSD([sQuery(id+"F8.wireOp",EDGE,"E14.1.2.0")])]})]});
            var Q14;
            {var subQ0=makeQuery(id+"F5.boolean.opBoolean","COPY",FACE,{"derivedFrom":makeQuery(id+"F5.opExtrude","SWEPT_FACE",FACE,{"disambiguationData":[OSD([sQuery(id+"F4.wireOp",EDGE,"E10.1.0.0")])]})});Q14=makeQuery(id+"F9.boolean.opBoolean","INTERSECT",EDGE,{"disambiguationData":[OD(1.0)],"derivedFrom":[makeQuery(id+"F7.boolean.opBoolean","SPLIT",FACE,{"disambiguationData":[TD([makeQuery(id+"F1.opExtrude","SWEPT_FACE",FACE,{"disambiguationData":[OSD([sQuery(id+"F0.wireOp",EDGE,"E0.bottom")])]}),subQ0,makeQuery(id+"F7.opExtrude","SWEPT_FACE",FACE,{"disambiguationData":[OSD([sQuery(id+"F6.wireOp",EDGE,"E11")])]})])],"derivedFrom":subQ0}),makeQuery(id+"F9.opExtrude","SWEPT_FACE",FACE,{"disambiguationData":[OSD([sQuery(id+"F8.wireOp",EDGE,"E14.1.2.0")])]})]});}
            var Q15;
            {var subQ0=makeQuery(id+"F5.boolean.opBoolean","COPY",FACE,{"derivedFrom":makeQuery(id+"F5.opExtrude","SWEPT_FACE",FACE,{"disambiguationData":[OSD([sQuery(id+"F4.wireOp",EDGE,"E10.1.0.0")])]})});Q15=makeQuery(id+"F9.boolean.opBoolean","INTERSECT",EDGE,{"disambiguationData":[OD(1.0)],"derivedFrom":[makeQuery(id+"F7.boolean.opBoolean","SPLIT",FACE,{"disambiguationData":[TD([subQ0,makeQuery(id+"F7.opExtrude","SWEPT_FACE",FACE,{"disambiguationData":[OSD([sQuery(id+"F6.wireOp",EDGE,"E11")])]}),makeQuery(id+"F7.opExtrude","SWEPT_FACE",FACE,{"disambiguationData":[OSD([sQuery(id+"F6.wireOp",EDGE,"E12.1.0.0")])]})])],"derivedFrom":subQ0}),makeQuery(id+"F9.opExtrude","SWEPT_FACE",FACE,{"disambiguationData":[OSD([sQuery(id+"F8.wireOp",EDGE,"E14.1.2.0")])]})]});}
            var Q16;
            Q16=makeQuery(id+"F7.boolean.opBoolean","INTERSECT",EDGE,{"disambiguationData":[OD(3.0)],"derivedFrom":[makeQuery(id+"F5.boolean.opBoolean","COPY",FACE,{"derivedFrom":makeQuery(id+"F5.opExtrude","SWEPT_FACE",FACE,{"disambiguationData":[OSD([sQuery(id+"F4.wireOp",EDGE,"E10.1.0.0")])]})}),makeQuery(id+"F7.opExtrude","SWEPT_FACE",FACE,{"disambiguationData":[OSD([sQuery(id+"F6.wireOp",EDGE,"E11")])]})]});
            var Q17;
            {var subQ0=makeQuery(id+"F5.boolean.opBoolean","COPY",FACE,{"derivedFrom":makeQuery(id+"F5.opExtrude","SWEPT_FACE",FACE,{"disambiguationData":[OSD([sQuery(id+"F4.wireOp",EDGE,"E10.1.0.0")])]})});Q17=makeQuery(id+"F9.boolean.opBoolean","INTERSECT",EDGE,{"disambiguationData":[OD(0.0)],"derivedFrom":[makeQuery(id+"F7.boolean.opBoolean","SPLIT",FACE,{"disambiguationData":[TD([subQ0,makeQuery(id+"F7.opExtrude","SWEPT_FACE",FACE,{"disambiguationData":[OSD([sQuery(id+"F6.wireOp",EDGE,"E11")])]}),makeQuery(id+"F7.opExtrude","SWEPT_FACE",FACE,{"disambiguationData":[OSD([sQuery(id+"F6.wireOp",EDGE,"E12.1.0.0")])]})])],"derivedFrom":subQ0}),makeQuery(id+"F9.opExtrude","SWEPT_FACE",FACE,{"disambiguationData":[OSD([sQuery(id+"F8.wireOp",EDGE,"E14.1.2.0")])]})]});}
            var Q18;
            Q18=makeQuery(id+"F7.boolean.opBoolean","INTERSECT",EDGE,{"disambiguationData":[OD(2.0)],"derivedFrom":[makeQuery(id+"F5.boolean.opBoolean","COPY",FACE,{"derivedFrom":makeQuery(id+"F5.opExtrude","SWEPT_FACE",FACE,{"disambiguationData":[OSD([sQuery(id+"F4.wireOp",EDGE,"E10.1.0.0")])]})}),makeQuery(id+"F7.opExtrude","SWEPT_FACE",FACE,{"disambiguationData":[OSD([sQuery(id+"F6.wireOp",EDGE,"E11")])]})]});
            var Q19;
            {var subQ0=makeQuery(id+"F5.boolean.opBoolean","COPY",FACE,{"derivedFrom":makeQuery(id+"F5.opExtrude","SWEPT_FACE",FACE,{"disambiguationData":[OSD([sQuery(id+"F4.wireOp",EDGE,"E10.1.1.0")])]})});Q19=makeQuery(id+"F9.boolean.opBoolean","INTERSECT",EDGE,{"disambiguationData":[OD(0.0)],"derivedFrom":[makeQuery(id+"F7.boolean.opBoolean","SPLIT",FACE,{"disambiguationData":[TD([makeQuery(id+"F1.opExtrude","SWEPT_FACE",FACE,{"disambiguationData":[OSD([sQuery(id+"F0.wireOp",EDGE,"E4")])]})])],"derivedFrom":subQ0}),makeQuery(id+"F9.opExtrude","SWEPT_FACE",FACE,{"disambiguationData":[OSD([sQuery(id+"F8.wireOp",EDGE,"E14.1.1.0")])]})]});}
            var Q20;
            Q20=makeQuery(id+"F7.boolean.opBoolean","INTERSECT",EDGE,{"disambiguationData":[OD(2.0)],"derivedFrom":[makeQuery(id+"F5.boolean.opBoolean","COPY",FACE,{"derivedFrom":makeQuery(id+"F5.opExtrude","SWEPT_FACE",FACE,{"disambiguationData":[OSD([sQuery(id+"F4.wireOp",EDGE,"E10.1.1.0")])]})}),makeQuery(id+"F7.opExtrude","SWEPT_FACE",FACE,{"disambiguationData":[OSD([sQuery(id+"F6.wireOp",EDGE,"E12.1.1.0")])]})]});
            var Q21;
            Q21=makeQuery(id+"F9.boolean.opBoolean","INTERSECT",EDGE,{"disambiguationData":[OD(1.0)],"derivedFrom":[makeQuery(id+"F7.boolean.opBoolean","COPY",FACE,{"disambiguationData":[OD(1.0)],"derivedFrom":makeQuery(id+"F7.opExtrude","SWEPT_FACE",FACE,{"disambiguationData":[OSD([sQuery(id+"F6.wireOp",EDGE,"E12.1.1.0")])]})}),makeQuery(id+"F9.opExtrude","SWEPT_FACE",FACE,{"disambiguationData":[OSD([sQuery(id+"F8.wireOp",EDGE,"E14.1.1.0")])]})]});
            var Q22;
            Q22=makeQuery(id+"F7.boolean.opBoolean","INTERSECT",EDGE,{"disambiguationData":[OD(0.0)],"derivedFrom":[makeQuery(id+"F5.boolean.opBoolean","COPY",FACE,{"derivedFrom":makeQuery(id+"F5.opExtrude","SWEPT_FACE",FACE,{"disambiguationData":[OSD([sQuery(id+"F4.wireOp",EDGE,"E10.1.1.0")])]})}),makeQuery(id+"F7.opExtrude","SWEPT_FACE",FACE,{"disambiguationData":[OSD([sQuery(id+"F6.wireOp",EDGE,"E12.1.1.0")])]})]});
            var Q23;
            {var subQ0=makeQuery(id+"F5.boolean.opBoolean","COPY",FACE,{"derivedFrom":makeQuery(id+"F5.opExtrude","SWEPT_FACE",FACE,{"disambiguationData":[OSD([sQuery(id+"F4.wireOp",EDGE,"E10.1.1.0")])]})});Q23=makeQuery(id+"F9.boolean.opBoolean","INTERSECT",EDGE,{"disambiguationData":[OD(1.0)],"derivedFrom":[makeQuery(id+"F7.boolean.opBoolean","SPLIT",FACE,{"disambiguationData":[TD([makeQuery(id+"F3.opExtrude","SWEPT_FACE",FACE,{"disambiguationData":[OSD([sQuery(id+"F2.wireOp",EDGE,"E5.bottom")])]})])],"derivedFrom":subQ0}),makeQuery(id+"F9.opExtrude","SWEPT_FACE",FACE,{"disambiguationData":[OSD([sQuery(id+"F8.wireOp",EDGE,"E14.1.1.0")])]})]});}
            var Q24;
            Q24=makeQuery(id+"F9.boolean.opBoolean","INTERSECT",EDGE,{"disambiguationData":[OD(0.0)],"derivedFrom":[makeQuery(id+"F7.boolean.opBoolean","COPY",FACE,{"disambiguationData":[OD(1.0)],"derivedFrom":makeQuery(id+"F7.opExtrude","SWEPT_FACE",FACE,{"disambiguationData":[OSD([sQuery(id+"F6.wireOp",EDGE,"E12.1.1.0")])]})}),makeQuery(id+"F9.opExtrude","SWEPT_FACE",FACE,{"disambiguationData":[OSD([sQuery(id+"F8.wireOp",EDGE,"E14.1.1.0")])]})]});
            var Q25;
            {var subQ0=makeQuery(id+"F5.boolean.opBoolean","COPY",FACE,{"derivedFrom":makeQuery(id+"F5.opExtrude","SWEPT_FACE",FACE,{"disambiguationData":[OSD([sQuery(id+"F4.wireOp",EDGE,"E10.1.1.0")])]})});Q25=makeQuery(id+"F9.boolean.opBoolean","INTERSECT",EDGE,{"disambiguationData":[OD(1.0)],"derivedFrom":[makeQuery(id+"F7.boolean.opBoolean","SPLIT",FACE,{"disambiguationData":[TD([makeQuery(id+"F1.opExtrude","SWEPT_FACE",FACE,{"disambiguationData":[OSD([sQuery(id+"F0.wireOp",EDGE,"E4")])]})])],"derivedFrom":subQ0}),makeQuery(id+"F9.opExtrude","SWEPT_FACE",FACE,{"disambiguationData":[OSD([sQuery(id+"F8.wireOp",EDGE,"E14.1.1.0")])]})]});}
            var Q26;
            Q26=makeQuery(id+"F7.boolean.opBoolean","INTERSECT",EDGE,{"disambiguationData":[OD(3.0)],"derivedFrom":[makeQuery(id+"F5.boolean.opBoolean","COPY",FACE,{"derivedFrom":makeQuery(id+"F5.opExtrude","SWEPT_FACE",FACE,{"disambiguationData":[OSD([sQuery(id+"F4.wireOp",EDGE,"E10.1.1.0")])]})}),makeQuery(id+"F7.opExtrude","SWEPT_FACE",FACE,{"disambiguationData":[OSD([sQuery(id+"F6.wireOp",EDGE,"E12.1.1.0")])]})]});
            var Q27;
            Q27=makeQuery(id+"F9.boolean.opBoolean","INTERSECT",EDGE,{"disambiguationData":[OD(1.0)],"derivedFrom":[makeQuery(id+"F7.boolean.opBoolean","COPY",FACE,{"disambiguationData":[OD(2.0)],"derivedFrom":makeQuery(id+"F7.opExtrude","SWEPT_FACE",FACE,{"disambiguationData":[OSD([sQuery(id+"F6.wireOp",EDGE,"E12.1.1.0")])]})}),makeQuery(id+"F9.opExtrude","SWEPT_FACE",FACE,{"disambiguationData":[OSD([sQuery(id+"F8.wireOp",EDGE,"E14.1.1.0")])]})]});
            var Q28;
            Q28=makeQuery(id+"F9.boolean.opBoolean","INTERSECT",EDGE,{"disambiguationData":[OD(0.0)],"derivedFrom":[makeQuery(id+"F7.boolean.opBoolean","COPY",FACE,{"disambiguationData":[OD(2.0)],"derivedFrom":makeQuery(id+"F7.opExtrude","SWEPT_FACE",FACE,{"disambiguationData":[OSD([sQuery(id+"F6.wireOp",EDGE,"E12.1.1.0")])]})}),makeQuery(id+"F9.opExtrude","SWEPT_FACE",FACE,{"disambiguationData":[OSD([sQuery(id+"F8.wireOp",EDGE,"E14.1.1.0")])]})]});
            var Q29;
            {var subQ0=makeQuery(id+"F5.boolean.opBoolean","COPY",FACE,{"derivedFrom":makeQuery(id+"F5.opExtrude","SWEPT_FACE",FACE,{"disambiguationData":[OSD([sQuery(id+"F4.wireOp",EDGE,"E10.1.1.0")])]})});Q29=makeQuery(id+"F9.boolean.opBoolean","INTERSECT",EDGE,{"disambiguationData":[OD(0.0)],"derivedFrom":[makeQuery(id+"F7.boolean.opBoolean","SPLIT",FACE,{"disambiguationData":[TD([makeQuery(id+"F3.opExtrude","SWEPT_FACE",FACE,{"disambiguationData":[OSD([sQuery(id+"F2.wireOp",EDGE,"E5.bottom")])]})])],"derivedFrom":subQ0}),makeQuery(id+"F9.opExtrude","SWEPT_FACE",FACE,{"disambiguationData":[OSD([sQuery(id+"F8.wireOp",EDGE,"E14.1.1.0")])]})]});}
            var Q30;
            Q30=makeQuery(id+"F7.boolean.opBoolean","INTERSECT",EDGE,{"disambiguationData":[OD(1.0)],"derivedFrom":[makeQuery(id+"F5.boolean.opBoolean","COPY",FACE,{"derivedFrom":makeQuery(id+"F5.opExtrude","SWEPT_FACE",FACE,{"disambiguationData":[OSD([sQuery(id+"F4.wireOp",EDGE,"E10.1.1.0")])]})}),makeQuery(id+"F7.opExtrude","SWEPT_FACE",FACE,{"disambiguationData":[OSD([sQuery(id+"F6.wireOp",EDGE,"E12.1.1.0")])]})]});
            var Q31;
            Q31=makeQuery(id+"F7.boolean.opBoolean","INTERSECT",EDGE,{"disambiguationData":[OD(3.0)],"derivedFrom":[makeQuery(id+"F5.boolean.opBoolean","COPY",FACE,{"derivedFrom":makeQuery(id+"F5.opExtrude","SWEPT_FACE",FACE,{"disambiguationData":[OSD([sQuery(id+"F4.wireOp",EDGE,"E10.2.1.0")])]})}),makeQuery(id+"F7.opExtrude","SWEPT_FACE",FACE,{"disambiguationData":[OSD([sQuery(id+"F6.wireOp",EDGE,"E12.2.1.0")])]})]});
            var Q32;
            Q32=makeQuery(id+"F9.boolean.opBoolean","INTERSECT",EDGE,{"disambiguationData":[OD(1.0)],"derivedFrom":[makeQuery(id+"F7.boolean.opBoolean","COPY",FACE,{"disambiguationData":[OD(1.0)],"derivedFrom":makeQuery(id+"F7.opExtrude","SWEPT_FACE",FACE,{"disambiguationData":[OSD([sQuery(id+"F6.wireOp",EDGE,"E12.2.1.0")])]})}),makeQuery(id+"F9.opExtrude","SWEPT_FACE",FACE,{"disambiguationData":[OSD([sQuery(id+"F8.wireOp",EDGE,"E13")])]})]});
            var Q33;
            {var subQ0=makeQuery(id+"F5.boolean.opBoolean","COPY",FACE,{"derivedFrom":makeQuery(id+"F5.opExtrude","SWEPT_FACE",FACE,{"disambiguationData":[OSD([sQuery(id+"F4.wireOp",EDGE,"E10.2.1.0")])]})});Q33=makeQuery(id+"F9.boolean.opBoolean","INTERSECT",EDGE,{"disambiguationData":[OD(1.0)],"derivedFrom":[makeQuery(id+"F7.boolean.opBoolean","SPLIT",FACE,{"disambiguationData":[TD([subQ0,makeQuery(id+"F7.opExtrude","SWEPT_FACE",FACE,{"disambiguationData":[OSD([sQuery(id+"F6.wireOp",EDGE,"E12.1.1.0")])]}),makeQuery(id+"F7.opExtrude","SWEPT_FACE",FACE,{"disambiguationData":[OSD([sQuery(id+"F6.wireOp",EDGE,"E12.2.1.0")])]})])],"derivedFrom":subQ0}),makeQuery(id+"F9.opExtrude","SWEPT_FACE",FACE,{"disambiguationData":[OSD([sQuery(id+"F8.wireOp",EDGE,"E13")])]})]});}
            var Q34;
            Q34=makeQuery(id+"F9.boolean.opBoolean","INTERSECT",EDGE,{"disambiguationData":[OD(1.0)],"derivedFrom":[makeQuery(id+"F7.boolean.opBoolean","COPY",FACE,{"disambiguationData":[OD(2.0)],"derivedFrom":makeQuery(id+"F7.opExtrude","SWEPT_FACE",FACE,{"disambiguationData":[OSD([sQuery(id+"F6.wireOp",EDGE,"E12.1.1.0")])]})}),makeQuery(id+"F9.opExtrude","SWEPT_FACE",FACE,{"disambiguationData":[OSD([sQuery(id+"F8.wireOp",EDGE,"E14.0.1.0")])]})]});
            var Q35;
            {var subQ0=makeQuery(id+"F5.boolean.opBoolean","COPY",FACE,{"derivedFrom":makeQuery(id+"F5.opExtrude","SWEPT_FACE",FACE,{"disambiguationData":[OSD([sQuery(id+"F4.wireOp",EDGE,"E10.2.1.0")])]})});Q35=makeQuery(id+"F9.boolean.opBoolean","INTERSECT",EDGE,{"disambiguationData":[OD(1.0)],"derivedFrom":[makeQuery(id+"F7.boolean.opBoolean","SPLIT",FACE,{"disambiguationData":[TD([subQ0,makeQuery(id+"F7.opExtrude","SWEPT_FACE",FACE,{"disambiguationData":[OSD([sQuery(id+"F6.wireOp",EDGE,"E12.1.1.0")])]}),makeQuery(id+"F7.opExtrude","SWEPT_FACE",FACE,{"disambiguationData":[OSD([sQuery(id+"F6.wireOp",EDGE,"E12.2.1.0")])]})])],"derivedFrom":subQ0}),makeQuery(id+"F9.opExtrude","SWEPT_FACE",FACE,{"disambiguationData":[OSD([sQuery(id+"F8.wireOp",EDGE,"E14.0.1.0")])]})]});}
            var Q36;
            Q36=makeQuery(id+"F7.boolean.opBoolean","INTERSECT",EDGE,{"disambiguationData":[OD(3.0)],"derivedFrom":[makeQuery(id+"F5.boolean.opBoolean","COPY",FACE,{"derivedFrom":makeQuery(id+"F5.opExtrude","SWEPT_FACE",FACE,{"disambiguationData":[OSD([sQuery(id+"F4.wireOp",EDGE,"E10.2.1.0")])]})}),makeQuery(id+"F7.opExtrude","SWEPT_FACE",FACE,{"disambiguationData":[OSD([sQuery(id+"F6.wireOp",EDGE,"E12.1.1.0")])]})]});
            var Q37;
            Q37=makeQuery(id+"F7.boolean.opBoolean","INTERSECT",EDGE,{"disambiguationData":[OD(1.0)],"derivedFrom":[makeQuery(id+"F5.boolean.opBoolean","COPY",FACE,{"derivedFrom":makeQuery(id+"F5.opExtrude","SWEPT_FACE",FACE,{"disambiguationData":[OSD([sQuery(id+"F4.wireOp",EDGE,"E10.2.1.0")])]})}),makeQuery(id+"F7.opExtrude","SWEPT_FACE",FACE,{"disambiguationData":[OSD([sQuery(id+"F6.wireOp",EDGE,"E12.1.1.0")])]})]});
            var Q38;
            {var subQ0=makeQuery(id+"F5.boolean.opBoolean","COPY",FACE,{"derivedFrom":makeQuery(id+"F5.opExtrude","SWEPT_FACE",FACE,{"disambiguationData":[OSD([sQuery(id+"F4.wireOp",EDGE,"E10.2.1.0")])]})});Q38=makeQuery(id+"F9.boolean.opBoolean","INTERSECT",EDGE,{"disambiguationData":[OD(1.0)],"derivedFrom":[makeQuery(id+"F7.boolean.opBoolean","SPLIT",FACE,{"disambiguationData":[TD([makeQuery(id+"F3.opExtrude","SWEPT_FACE",FACE,{"disambiguationData":[OSD([sQuery(id+"F2.wireOp",EDGE,"E5.bottom")])]}),subQ0,makeQuery(id+"F7.opExtrude","SWEPT_FACE",FACE,{"disambiguationData":[OSD([sQuery(id+"F6.wireOp",EDGE,"E12.1.1.0")])]})])],"derivedFrom":subQ0}),makeQuery(id+"F9.opExtrude","SWEPT_FACE",FACE,{"disambiguationData":[OSD([sQuery(id+"F8.wireOp",EDGE,"E14.0.1.0")])]})]});}
            var Q39;
            {var subQ0=makeQuery(id+"F5.boolean.opBoolean","COPY",FACE,{"derivedFrom":makeQuery(id+"F5.opExtrude","SWEPT_FACE",FACE,{"disambiguationData":[OSD([sQuery(id+"F4.wireOp",EDGE,"E10.2.1.0")])]})});Q39=makeQuery(id+"F9.boolean.opBoolean","INTERSECT",EDGE,{"disambiguationData":[OD(0.0)],"derivedFrom":[makeQuery(id+"F7.boolean.opBoolean","SPLIT",FACE,{"disambiguationData":[TD([subQ0,makeQuery(id+"F7.opExtrude","SWEPT_FACE",FACE,{"disambiguationData":[OSD([sQuery(id+"F6.wireOp",EDGE,"E12.1.1.0")])]}),makeQuery(id+"F7.opExtrude","SWEPT_FACE",FACE,{"disambiguationData":[OSD([sQuery(id+"F6.wireOp",EDGE,"E12.2.1.0")])]})])],"derivedFrom":subQ0}),makeQuery(id+"F9.opExtrude","SWEPT_FACE",FACE,{"disambiguationData":[OSD([sQuery(id+"F8.wireOp",EDGE,"E14.0.1.0")])]})]});}
            var Q40;
            Q40=makeQuery(id+"F9.boolean.opBoolean","INTERSECT",EDGE,{"disambiguationData":[OD(0.0)],"derivedFrom":[makeQuery(id+"F7.boolean.opBoolean","COPY",FACE,{"disambiguationData":[OD(0.0)],"derivedFrom":makeQuery(id+"F7.opExtrude","SWEPT_FACE",FACE,{"disambiguationData":[OSD([sQuery(id+"F6.wireOp",EDGE,"E12.1.1.0")])]})}),makeQuery(id+"F9.opExtrude","SWEPT_FACE",FACE,{"disambiguationData":[OSD([sQuery(id+"F8.wireOp",EDGE,"E14.0.1.0")])]})]});
            var Q41;
            Q41=makeQuery(id+"F7.boolean.opBoolean","INTERSECT",EDGE,{"disambiguationData":[OD(2.0)],"derivedFrom":[makeQuery(id+"F5.boolean.opBoolean","COPY",FACE,{"derivedFrom":makeQuery(id+"F5.opExtrude","SWEPT_FACE",FACE,{"disambiguationData":[OSD([sQuery(id+"F4.wireOp",EDGE,"E10.2.1.0")])]})}),makeQuery(id+"F7.opExtrude","SWEPT_FACE",FACE,{"disambiguationData":[OSD([sQuery(id+"F6.wireOp",EDGE,"E12.1.1.0")])]})]});
            var Q42;
            Q42=makeQuery(id+"F7.boolean.opBoolean","INTERSECT",EDGE,{"disambiguationData":[OD(0.0)],"derivedFrom":[makeQuery(id+"F5.boolean.opBoolean","COPY",FACE,{"derivedFrom":makeQuery(id+"F5.opExtrude","SWEPT_FACE",FACE,{"disambiguationData":[OSD([sQuery(id+"F4.wireOp",EDGE,"E10.2.1.0")])]})}),makeQuery(id+"F7.opExtrude","SWEPT_FACE",FACE,{"disambiguationData":[OSD([sQuery(id+"F6.wireOp",EDGE,"E12.1.1.0")])]})]});
            var Q43;
            Q43=makeQuery(id+"F9.boolean.opBoolean","INTERSECT",EDGE,{"disambiguationData":[OD(1.0)],"derivedFrom":[makeQuery(id+"F7.boolean.opBoolean","COPY",FACE,{"disambiguationData":[OD(0.0)],"derivedFrom":makeQuery(id+"F7.opExtrude","SWEPT_FACE",FACE,{"disambiguationData":[OSD([sQuery(id+"F6.wireOp",EDGE,"E12.1.1.0")])]})}),makeQuery(id+"F9.opExtrude","SWEPT_FACE",FACE,{"disambiguationData":[OSD([sQuery(id+"F8.wireOp",EDGE,"E14.0.1.0")])]})]});
            var Q44;
            {var subQ0=makeQuery(id+"F5.boolean.opBoolean","COPY",FACE,{"derivedFrom":makeQuery(id+"F5.opExtrude","SWEPT_FACE",FACE,{"disambiguationData":[OSD([sQuery(id+"F4.wireOp",EDGE,"E10.2.1.0")])]})});Q44=makeQuery(id+"F9.boolean.opBoolean","INTERSECT",EDGE,{"disambiguationData":[OD(0.0)],"derivedFrom":[makeQuery(id+"F7.boolean.opBoolean","SPLIT",FACE,{"disambiguationData":[TD([makeQuery(id+"F3.opExtrude","SWEPT_FACE",FACE,{"disambiguationData":[OSD([sQuery(id+"F2.wireOp",EDGE,"E5.bottom")])]}),subQ0,makeQuery(id+"F7.opExtrude","SWEPT_FACE",FACE,{"disambiguationData":[OSD([sQuery(id+"F6.wireOp",EDGE,"E12.1.1.0")])]})])],"derivedFrom":subQ0}),makeQuery(id+"F9.opExtrude","SWEPT_FACE",FACE,{"disambiguationData":[OSD([sQuery(id+"F8.wireOp",EDGE,"E14.0.1.0")])]})]});}
            var Q45;
            Q45=makeQuery(id+"F9.boolean.opBoolean","INTERSECT",EDGE,{"disambiguationData":[OD(0.0)],"derivedFrom":[makeQuery(id+"F7.boolean.opBoolean","COPY",FACE,{"disambiguationData":[OD(2.0)],"derivedFrom":makeQuery(id+"F7.opExtrude","SWEPT_FACE",FACE,{"disambiguationData":[OSD([sQuery(id+"F6.wireOp",EDGE,"E12.1.1.0")])]})}),makeQuery(id+"F9.opExtrude","SWEPT_FACE",FACE,{"disambiguationData":[OSD([sQuery(id+"F8.wireOp",EDGE,"E14.0.1.0")])]})]});
            var Q46;
            Q46=makeQuery(id+"F9.boolean.opBoolean","INTERSECT",EDGE,{"disambiguationData":[OD(1.0)],"derivedFrom":[makeQuery(id+"F7.boolean.opBoolean","COPY",FACE,{"disambiguationData":[OD(0.0)],"derivedFrom":makeQuery(id+"F7.opExtrude","SWEPT_FACE",FACE,{"disambiguationData":[OSD([sQuery(id+"F6.wireOp",EDGE,"E12.1.0.0")])]})}),makeQuery(id+"F9.opExtrude","SWEPT_FACE",FACE,{"disambiguationData":[OSD([sQuery(id+"F8.wireOp",EDGE,"E14.1.1.0")])]})]});
            var Q47;
            Q47=makeQuery(id+"F7.boolean.opBoolean","INTERSECT",EDGE,{"disambiguationData":[OD(2.0)],"derivedFrom":[makeQuery(id+"F5.boolean.opBoolean","COPY",FACE,{"derivedFrom":makeQuery(id+"F5.opExtrude","SWEPT_FACE",FACE,{"disambiguationData":[OSD([sQuery(id+"F4.wireOp",EDGE,"E10.1.0.0")])]})}),makeQuery(id+"F7.opExtrude","SWEPT_FACE",FACE,{"disambiguationData":[OSD([sQuery(id+"F6.wireOp",EDGE,"E12.1.0.0")])]})]});
            var Q48;
            Q48=makeQuery(id+"F7.boolean.opBoolean","INTERSECT",EDGE,{"disambiguationData":[OD(3.0)],"derivedFrom":[makeQuery(id+"F5.boolean.opBoolean","COPY",FACE,{"derivedFrom":makeQuery(id+"F5.opExtrude","SWEPT_FACE",FACE,{"disambiguationData":[OSD([sQuery(id+"F4.wireOp",EDGE,"E10.1.0.0")])]})}),makeQuery(id+"F7.opExtrude","SWEPT_FACE",FACE,{"disambiguationData":[OSD([sQuery(id+"F6.wireOp",EDGE,"E12.1.0.0")])]})]});
            var Q49;
            {var subQ0=makeQuery(id+"F5.boolean.opBoolean","COPY",FACE,{"derivedFrom":makeQuery(id+"F5.opExtrude","SWEPT_FACE",FACE,{"disambiguationData":[OSD([sQuery(id+"F4.wireOp",EDGE,"E10.1.0.0")])]})});Q49=makeQuery(id+"F9.boolean.opBoolean","INTERSECT",EDGE,{"disambiguationData":[OD(1.0)],"derivedFrom":[makeQuery(id+"F7.boolean.opBoolean","SPLIT",FACE,{"disambiguationData":[TD([subQ0,makeQuery(id+"F7.opExtrude","SWEPT_FACE",FACE,{"disambiguationData":[OSD([sQuery(id+"F6.wireOp",EDGE,"E11")])]}),makeQuery(id+"F7.opExtrude","SWEPT_FACE",FACE,{"disambiguationData":[OSD([sQuery(id+"F6.wireOp",EDGE,"E12.1.0.0")])]})])],"derivedFrom":subQ0}),makeQuery(id+"F9.opExtrude","SWEPT_FACE",FACE,{"disambiguationData":[OSD([sQuery(id+"F8.wireOp",EDGE,"E14.1.1.0")])]})]});}
            var Q50;
            Q50=makeQuery(id+"F9.boolean.opBoolean","INTERSECT",EDGE,{"disambiguationData":[OD(1.0)],"derivedFrom":[makeQuery(id+"F7.boolean.opBoolean","COPY",FACE,{"disambiguationData":[OD(1.0)],"derivedFrom":makeQuery(id+"F7.opExtrude","SWEPT_FACE",FACE,{"disambiguationData":[OSD([sQuery(id+"F6.wireOp",EDGE,"E12.1.0.0")])]})}),makeQuery(id+"F9.opExtrude","SWEPT_FACE",FACE,{"disambiguationData":[OSD([sQuery(id+"F8.wireOp",EDGE,"E14.1.1.0")])]})]});
            var Q51;
            Q51=makeQuery(id+"F9.boolean.opBoolean","INTERSECT",EDGE,{"disambiguationData":[OD(0.0)],"derivedFrom":[makeQuery(id+"F7.boolean.opBoolean","COPY",FACE,{"disambiguationData":[OD(1.0)],"derivedFrom":makeQuery(id+"F7.opExtrude","SWEPT_FACE",FACE,{"disambiguationData":[OSD([sQuery(id+"F6.wireOp",EDGE,"E12.1.0.0")])]})}),makeQuery(id+"F9.opExtrude","SWEPT_FACE",FACE,{"disambiguationData":[OSD([sQuery(id+"F8.wireOp",EDGE,"E14.1.1.0")])]})]});
            var Q52;
            {var subQ0=makeQuery(id+"F5.boolean.opBoolean","COPY",FACE,{"derivedFrom":makeQuery(id+"F5.opExtrude","SWEPT_FACE",FACE,{"disambiguationData":[OSD([sQuery(id+"F4.wireOp",EDGE,"E10.1.0.0")])]})});Q52=makeQuery(id+"F9.boolean.opBoolean","INTERSECT",EDGE,{"disambiguationData":[OD(0.0)],"derivedFrom":[makeQuery(id+"F7.boolean.opBoolean","SPLIT",FACE,{"disambiguationData":[TD([makeQuery(id+"F1.opExtrude","SWEPT_FACE",FACE,{"disambiguationData":[OSD([sQuery(id+"F0.wireOp",EDGE,"E4")])]}),makeQuery(id+"F3.opExtrude","SWEPT_FACE",FACE,{"disambiguationData":[OSD([sQuery(id+"F2.wireOp",EDGE,"E6.bottom")])]}),subQ0,makeQuery(id+"F7.opExtrude","SWEPT_FACE",FACE,{"disambiguationData":[OSD([sQuery(id+"F6.wireOp",EDGE,"E12.1.0.0")])]})])],"derivedFrom":subQ0}),makeQuery(id+"F9.opExtrude","SWEPT_FACE",FACE,{"disambiguationData":[OSD([sQuery(id+"F8.wireOp",EDGE,"E14.1.1.0")])]})]});}
            var Q53;
            {var subQ0=makeQuery(id+"F5.boolean.opBoolean","COPY",FACE,{"derivedFrom":makeQuery(id+"F5.opExtrude","SWEPT_FACE",FACE,{"disambiguationData":[OSD([sQuery(id+"F4.wireOp",EDGE,"E10.1.0.0")])]})});Q53=makeQuery(id+"F9.boolean.opBoolean","INTERSECT",EDGE,{"disambiguationData":[OD(1.0)],"derivedFrom":[makeQuery(id+"F7.boolean.opBoolean","SPLIT",FACE,{"disambiguationData":[TD([makeQuery(id+"F1.opExtrude","SWEPT_FACE",FACE,{"disambiguationData":[OSD([sQuery(id+"F0.wireOp",EDGE,"E4")])]}),makeQuery(id+"F3.opExtrude","SWEPT_FACE",FACE,{"disambiguationData":[OSD([sQuery(id+"F2.wireOp",EDGE,"E6.bottom")])]}),subQ0,makeQuery(id+"F7.opExtrude","SWEPT_FACE",FACE,{"disambiguationData":[OSD([sQuery(id+"F6.wireOp",EDGE,"E12.1.0.0")])]})])],"derivedFrom":subQ0}),makeQuery(id+"F9.opExtrude","SWEPT_FACE",FACE,{"disambiguationData":[OSD([sQuery(id+"F8.wireOp",EDGE,"E14.1.1.0")])]})]});}
            var Q54;
            Q54=makeQuery(id+"F7.boolean.opBoolean","INTERSECT",EDGE,{"disambiguationData":[OD(0.0)],"derivedFrom":[makeQuery(id+"F5.boolean.opBoolean","COPY",FACE,{"derivedFrom":makeQuery(id+"F5.opExtrude","SWEPT_FACE",FACE,{"disambiguationData":[OSD([sQuery(id+"F4.wireOp",EDGE,"E10.1.0.0")])]})}),makeQuery(id+"F7.opExtrude","SWEPT_FACE",FACE,{"disambiguationData":[OSD([sQuery(id+"F6.wireOp",EDGE,"E12.1.0.0")])]})]});
            var Q55;
            Q55=makeQuery(id+"F7.boolean.opBoolean","INTERSECT",EDGE,{"disambiguationData":[OD(1.0)],"derivedFrom":[makeQuery(id+"F5.boolean.opBoolean","COPY",FACE,{"derivedFrom":makeQuery(id+"F5.opExtrude","SWEPT_FACE",FACE,{"disambiguationData":[OSD([sQuery(id+"F4.wireOp",EDGE,"E10.1.0.0")])]})}),makeQuery(id+"F7.opExtrude","SWEPT_FACE",FACE,{"disambiguationData":[OSD([sQuery(id+"F6.wireOp",EDGE,"E12.1.0.0")])]})]});
            var Q56;
            Q56=makeQuery(id+"F9.boolean.opBoolean","INTERSECT",EDGE,{"disambiguationData":[OD(0.0)],"derivedFrom":[makeQuery(id+"F7.boolean.opBoolean","COPY",FACE,{"disambiguationData":[OD(1.0)],"derivedFrom":makeQuery(id+"F7.opExtrude","SWEPT_FACE",FACE,{"disambiguationData":[OSD([sQuery(id+"F6.wireOp",EDGE,"E12.2.1.0")])]})}),makeQuery(id+"F9.opExtrude","SWEPT_FACE",FACE,{"disambiguationData":[OSD([sQuery(id+"F8.wireOp",EDGE,"E13")])]})]});
            var Q57;
            {var subQ0=makeQuery(id+"F5.boolean.opBoolean","COPY",FACE,{"derivedFrom":makeQuery(id+"F5.opExtrude","SWEPT_FACE",FACE,{"disambiguationData":[OSD([sQuery(id+"F4.wireOp",EDGE,"E10.2.1.0")])]})});Q57=makeQuery(id+"F9.boolean.opBoolean","INTERSECT",EDGE,{"disambiguationData":[OD(0.0)],"derivedFrom":[makeQuery(id+"F7.boolean.opBoolean","SPLIT",FACE,{"disambiguationData":[TD([makeQuery(id+"F3.opExtrude","SWEPT_FACE",FACE,{"disambiguationData":[OSD([sQuery(id+"F2.wireOp",EDGE,"E7")])]}),subQ0,makeQuery(id+"F7.opExtrude","SWEPT_FACE",FACE,{"disambiguationData":[OSD([sQuery(id+"F6.wireOp",EDGE,"E12.2.1.0")])]})])],"derivedFrom":subQ0}),makeQuery(id+"F9.opExtrude","SWEPT_FACE",FACE,{"disambiguationData":[OSD([sQuery(id+"F8.wireOp",EDGE,"E13")])]})]});}
            var Q58;
            Q58=makeQuery(id+"F7.boolean.opBoolean","INTERSECT",EDGE,{"disambiguationData":[OD(1.0)],"derivedFrom":[makeQuery(id+"F5.boolean.opBoolean","COPY",FACE,{"derivedFrom":makeQuery(id+"F5.opExtrude","SWEPT_FACE",FACE,{"disambiguationData":[OSD([sQuery(id+"F4.wireOp",EDGE,"E10.2.1.0")])]})}),makeQuery(id+"F7.opExtrude","SWEPT_FACE",FACE,{"disambiguationData":[OSD([sQuery(id+"F6.wireOp",EDGE,"E12.2.1.0")])]})]});
            var Q59;
            Q59=makeQuery(id+"F7.boolean.opBoolean","INTERSECT",EDGE,{"disambiguationData":[OD(0.0)],"derivedFrom":[makeQuery(id+"F5.boolean.opBoolean","COPY",FACE,{"derivedFrom":makeQuery(id+"F5.opExtrude","SWEPT_FACE",FACE,{"disambiguationData":[OSD([sQuery(id+"F4.wireOp",EDGE,"E10.2.1.0")])]})}),makeQuery(id+"F7.opExtrude","SWEPT_FACE",FACE,{"disambiguationData":[OSD([sQuery(id+"F6.wireOp",EDGE,"E12.2.1.0")])]})]});
            var Q60;
            {var subQ0=makeQuery(id+"F5.boolean.opBoolean","COPY",FACE,{"derivedFrom":makeQuery(id+"F5.opExtrude","SWEPT_FACE",FACE,{"disambiguationData":[OSD([sQuery(id+"F4.wireOp",EDGE,"E10.2.1.0")])]})});Q60=makeQuery(id+"F9.boolean.opBoolean","INTERSECT",EDGE,{"disambiguationData":[OD(1.0)],"derivedFrom":[makeQuery(id+"F7.boolean.opBoolean","SPLIT",FACE,{"disambiguationData":[TD([makeQuery(id+"F3.opExtrude","SWEPT_FACE",FACE,{"disambiguationData":[OSD([sQuery(id+"F2.wireOp",EDGE,"E7")])]}),subQ0,makeQuery(id+"F7.opExtrude","SWEPT_FACE",FACE,{"disambiguationData":[OSD([sQuery(id+"F6.wireOp",EDGE,"E12.2.1.0")])]})])],"derivedFrom":subQ0}),makeQuery(id+"F9.opExtrude","SWEPT_FACE",FACE,{"disambiguationData":[OSD([sQuery(id+"F8.wireOp",EDGE,"E13")])]})]});}
            var Q61;
            Q61=makeQuery(id+"F9.boolean.opBoolean","INTERSECT",EDGE,{"disambiguationData":[OD(1.0)],"derivedFrom":[makeQuery(id+"F7.boolean.opBoolean","COPY",FACE,{"disambiguationData":[OD(0.0)],"derivedFrom":makeQuery(id+"F7.opExtrude","SWEPT_FACE",FACE,{"disambiguationData":[OSD([sQuery(id+"F6.wireOp",EDGE,"E12.2.1.0")])]})}),makeQuery(id+"F9.opExtrude","SWEPT_FACE",FACE,{"disambiguationData":[OSD([sQuery(id+"F8.wireOp",EDGE,"E13")])]})]});
            var Q62;
            Q62=makeQuery(id+"F9.boolean.opBoolean","INTERSECT",EDGE,{"disambiguationData":[OD(0.0)],"derivedFrom":[makeQuery(id+"F7.boolean.opBoolean","COPY",FACE,{"disambiguationData":[OD(0.0)],"derivedFrom":makeQuery(id+"F7.opExtrude","SWEPT_FACE",FACE,{"disambiguationData":[OSD([sQuery(id+"F6.wireOp",EDGE,"E12.1.0.0")])]})}),makeQuery(id+"F9.opExtrude","SWEPT_FACE",FACE,{"disambiguationData":[OSD([sQuery(id+"F8.wireOp",EDGE,"E14.1.1.0")])]})]});
            var Q63;
            Q63=makeQuery(id+"F9.boolean.opBoolean","INTERSECT",EDGE,{"disambiguationData":[OD(1.0)],"derivedFrom":[makeQuery(id+"F7.boolean.opBoolean","COPY",FACE,{"disambiguationData":[OD(2.0)],"derivedFrom":makeQuery(id+"F7.opExtrude","SWEPT_FACE",FACE,{"disambiguationData":[OSD([sQuery(id+"F6.wireOp",EDGE,"E11")])]})}),makeQuery(id+"F9.opExtrude","SWEPT_FACE",FACE,{"disambiguationData":[OSD([sQuery(id+"F8.wireOp",EDGE,"E14.2.2.0")])]})]});
            var Q64;
            Q64=makeQuery(id+"F9.boolean.opBoolean","INTERSECT",EDGE,{"disambiguationData":[OD(0.0)],"derivedFrom":[makeQuery(id+"F7.boolean.opBoolean","COPY",FACE,{"disambiguationData":[OD(2.0)],"derivedFrom":makeQuery(id+"F7.opExtrude","SWEPT_FACE",FACE,{"disambiguationData":[OSD([sQuery(id+"F6.wireOp",EDGE,"E11")])]})}),makeQuery(id+"F9.opExtrude","SWEPT_FACE",FACE,{"disambiguationData":[OSD([sQuery(id+"F8.wireOp",EDGE,"E14.2.2.0")])]})]});
            var Q65;
            {var subQ0=makeQuery(id+"F5.boolean.opBoolean","COPY",FACE,{"derivedFrom":makeQuery(id+"F5.opExtrude","SWEPT_FACE",FACE,{"disambiguationData":[OSD([sQuery(id+"F4.wireOp",EDGE,"E9")])]})});Q65=makeQuery(id+"F9.boolean.opBoolean","INTERSECT",EDGE,{"disambiguationData":[OD(1.0)],"derivedFrom":[makeQuery(id+"F7.boolean.opBoolean","SPLIT",FACE,{"disambiguationData":[TD([makeQuery(id+"F1.opExtrude","SWEPT_FACE",FACE,{"disambiguationData":[OSD([sQuery(id+"F0.wireOp",EDGE,"E0.bottom")])]})])],"derivedFrom":subQ0}),makeQuery(id+"F9.opExtrude","SWEPT_FACE",FACE,{"disambiguationData":[OSD([sQuery(id+"F8.wireOp",EDGE,"E14.2.2.0")])]})]});}
            var Q66;
            Q66=makeQuery(id+"F7.boolean.opBoolean","INTERSECT",EDGE,{"disambiguationData":[OD(1.0)],"derivedFrom":[makeQuery(id+"F5.boolean.opBoolean","COPY",FACE,{"derivedFrom":makeQuery(id+"F5.opExtrude","SWEPT_FACE",FACE,{"disambiguationData":[OSD([sQuery(id+"F4.wireOp",EDGE,"E9")])]})}),makeQuery(id+"F7.opExtrude","SWEPT_FACE",FACE,{"disambiguationData":[OSD([sQuery(id+"F6.wireOp",EDGE,"E11")])]})]});
            var Q67;
            Q67=makeQuery(id+"F7.boolean.opBoolean","INTERSECT",EDGE,{"disambiguationData":[OD(3.0)],"derivedFrom":[makeQuery(id+"F5.boolean.opBoolean","COPY",FACE,{"derivedFrom":makeQuery(id+"F5.opExtrude","SWEPT_FACE",FACE,{"disambiguationData":[OSD([sQuery(id+"F4.wireOp",EDGE,"E9")])]})}),makeQuery(id+"F7.opExtrude","SWEPT_FACE",FACE,{"disambiguationData":[OSD([sQuery(id+"F6.wireOp",EDGE,"E11")])]})]});
            var Q68;
            {var subQ0=makeQuery(id+"F5.boolean.opBoolean","COPY",FACE,{"derivedFrom":makeQuery(id+"F5.opExtrude","SWEPT_FACE",FACE,{"disambiguationData":[OSD([sQuery(id+"F4.wireOp",EDGE,"E10.1.0.0")])]})});Q68=makeQuery(id+"F9.boolean.opBoolean","INTERSECT",EDGE,{"disambiguationData":[OD(0.0)],"derivedFrom":[makeQuery(id+"F7.boolean.opBoolean","SPLIT",FACE,{"disambiguationData":[TD([subQ0,makeQuery(id+"F7.opExtrude","SWEPT_FACE",FACE,{"disambiguationData":[OSD([sQuery(id+"F6.wireOp",EDGE,"E11")])]}),makeQuery(id+"F7.opExtrude","SWEPT_FACE",FACE,{"disambiguationData":[OSD([sQuery(id+"F6.wireOp",EDGE,"E12.1.0.0")])]})])],"derivedFrom":subQ0}),makeQuery(id+"F9.opExtrude","SWEPT_FACE",FACE,{"disambiguationData":[OSD([sQuery(id+"F8.wireOp",EDGE,"E14.1.1.0")])]})]});}
            var Q69;
            {var subQ0=makeQuery(id+"F5.boolean.opBoolean","COPY",FACE,{"derivedFrom":makeQuery(id+"F5.opExtrude","SWEPT_FACE",FACE,{"disambiguationData":[OSD([sQuery(id+"F4.wireOp",EDGE,"E10.2.1.0")])]})});Q69=makeQuery(id+"F9.boolean.opBoolean","INTERSECT",EDGE,{"disambiguationData":[OD(0.0)],"derivedFrom":[makeQuery(id+"F7.boolean.opBoolean","SPLIT",FACE,{"disambiguationData":[TD([subQ0,makeQuery(id+"F7.opExtrude","SWEPT_FACE",FACE,{"disambiguationData":[OSD([sQuery(id+"F6.wireOp",EDGE,"E12.1.1.0")])]}),makeQuery(id+"F7.opExtrude","SWEPT_FACE",FACE,{"disambiguationData":[OSD([sQuery(id+"F6.wireOp",EDGE,"E12.2.1.0")])]})])],"derivedFrom":subQ0}),makeQuery(id+"F9.opExtrude","SWEPT_FACE",FACE,{"disambiguationData":[OSD([sQuery(id+"F8.wireOp",EDGE,"E13")])]})]});}
            var Q70;
            Q70=makeQuery(id+"F9.boolean.opBoolean","INTERSECT",EDGE,{"disambiguationData":[OD(0.0)],"derivedFrom":[makeQuery(id+"F7.boolean.opBoolean","COPY",FACE,{"disambiguationData":[OD(0.0)],"derivedFrom":makeQuery(id+"F7.opExtrude","SWEPT_FACE",FACE,{"disambiguationData":[OSD([sQuery(id+"F6.wireOp",EDGE,"E12.2.1.0")])]})}),makeQuery(id+"F9.opExtrude","SWEPT_FACE",FACE,{"disambiguationData":[OSD([sQuery(id+"F8.wireOp",EDGE,"E13")])]})]});
            var Q71;
            Q71=makeQuery(id+"F7.boolean.opBoolean","INTERSECT",EDGE,{"disambiguationData":[OD(2.0)],"derivedFrom":[makeQuery(id+"F5.boolean.opBoolean","COPY",FACE,{"derivedFrom":makeQuery(id+"F5.opExtrude","SWEPT_FACE",FACE,{"disambiguationData":[OSD([sQuery(id+"F4.wireOp",EDGE,"E10.2.1.0")])]})}),makeQuery(id+"F7.opExtrude","SWEPT_FACE",FACE,{"disambiguationData":[OSD([sQuery(id+"F6.wireOp",EDGE,"E12.2.1.0")])]})]});
            fillet(context, id + "F14", {"entities" : qUnion([Q0, Q1, Q2, Q3, Q4, Q5, Q6, Q7, Q8, Q9, Q10, Q11, Q12, Q13, Q14, Q15, Q16, Q17, Q18, Q19, Q20, Q21, Q22, Q23, Q24, Q25, Q26, Q27, Q28, Q29, Q30, Q31, Q32, Q33, Q34, Q35, Q36, Q37, Q38, Q39, Q40, Q41, Q42, Q43, Q44, Q45, Q46, Q47, Q48, Q49, Q50, Q51, Q52, Q53, Q54, Q55, Q56, Q57, Q58, Q59, Q60, Q61, Q62, Q63, Q64, Q65, Q66, Q67, Q68, Q69, Q70, Q71]), "radius" : 2.54 * mm, "tangentPropagation" : true, "allowEdgeOverflow" : false});
        }
    });
